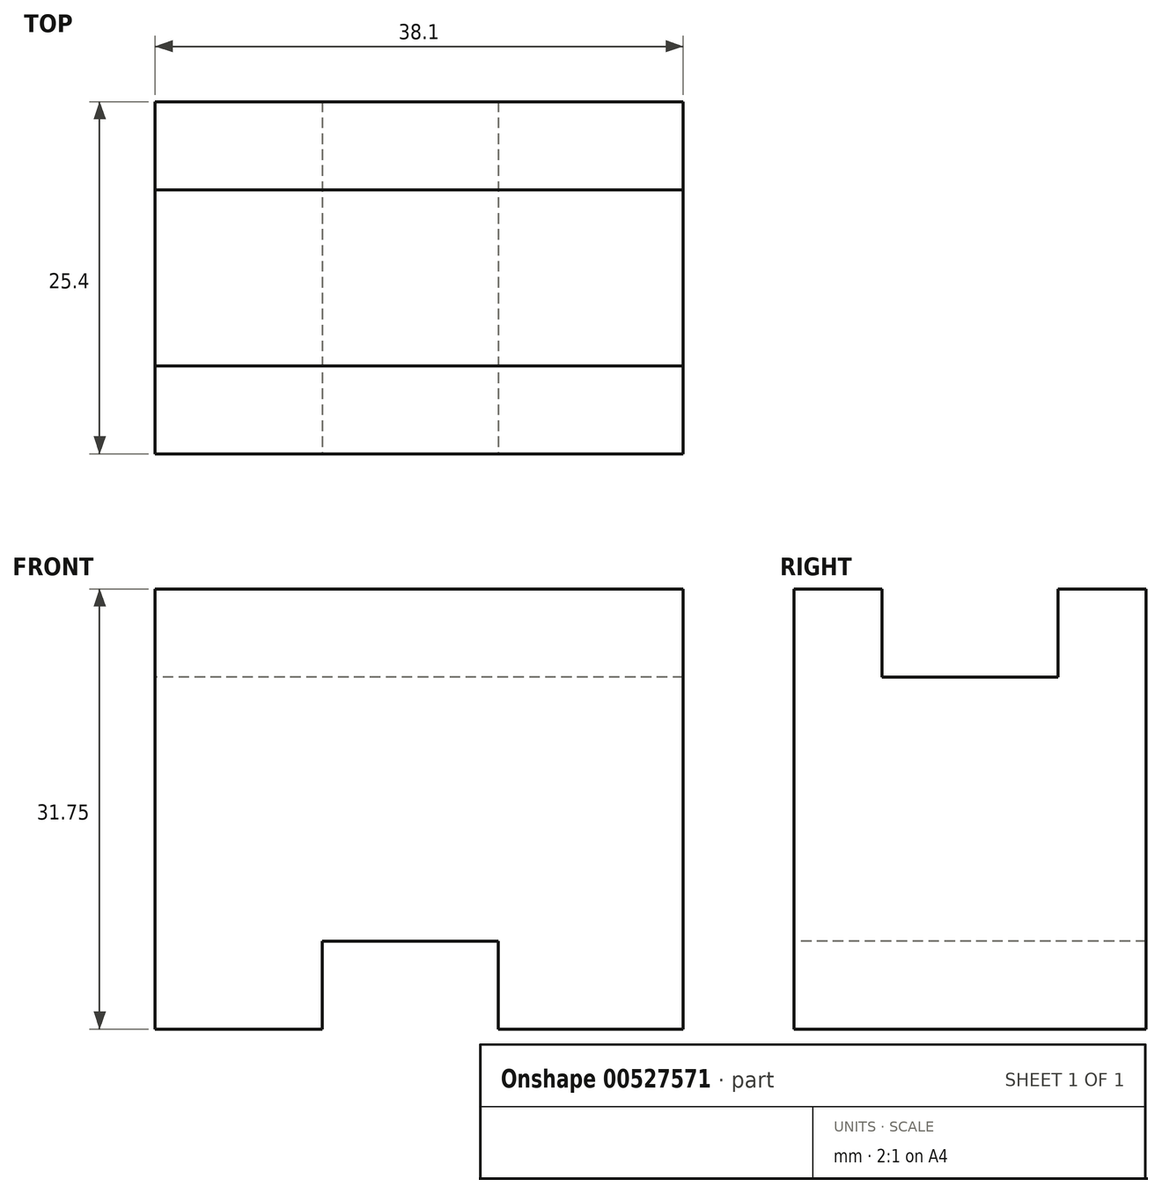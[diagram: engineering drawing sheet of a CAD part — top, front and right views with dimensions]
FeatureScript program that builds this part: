
annotation { "Feature Type Name" : "Feature", "Feature Type Description" : "" }
export const myFeature = defineFeature(function(context is Context, id is Id, definition is map)
    precondition{}
    {
        {
            var Q0;
            Q0=qCreatedBy(makeId("Right.planeOp"),FACE);
            var sketch = newSketch(context, id + "F0", { "sketchPlane" : qUnion([Q0])});
            skLineSegment(sketch, "E0", {"start": v(0, 0) * mm, "end": v(0, 31.75) * mm});
            skLineSegment(sketch, "E1", {"start": v(0, 31.75) * mm, "end": v(6.35, 31.75) * mm});
            skLineSegment(sketch, "E2", {"start": v(6.35, 31.75) * mm, "end": v(6.35, 25.4) * mm});
            skLineSegment(sketch, "E3", {"start": v(6.35, 25.4) * mm, "end": v(19.05, 25.4) * mm});
            skLineSegment(sketch, "E4", {"start": v(19.05, 25.4) * mm, "end": v(19.05, 31.75) * mm});
            skLineSegment(sketch, "E5", {"start": v(19.05, 31.75) * mm, "end": v(25.4, 31.75) * mm});
            skLineSegment(sketch, "E6", {"start": v(25.4, 31.75) * mm, "end": v(25.4, 0) * mm});
            skLineSegment(sketch, "E7", {"start": v(0, 0) * mm, "end": v(25.4, 0) * mm});
            skSolve(sketch);
        }
        {
            var Q0;
            Q0=makeQuery(id+"F0.imprint","IMPRINT",FACE,{"disambiguationData":[TD([[makeQuery(id+"F0.imprint","IMPRINT",EDGE,{"derivedFrom":sQuery(id+"F0.wireOp",EDGE,"E0")}),-1.0]])]});
            extrude(context, id + "F1", {"entities" : qUnion([Q0]), "depth" : 38.1 * mm, "offsetDistance" : 25.4 * mm});
        }
        {
            var Q0;
            Q0=makeQuery(id+"F1.opExtrude","SWEPT_FACE",FACE,{"disambiguationData":[OSD([sQuery(id+"F0.wireOp",EDGE,"E0")])]});
            var sketch = newSketch(context, id + "F2", { "sketchPlane" : qUnion([Q0])});
            skLineSegment(sketch, "E8", {"start": v(12.07, 0) * mm, "end": v(12.07, 6.35) * mm});
            skLineSegment(sketch, "E9", {"start": v(12.07, 6.35) * mm, "end": v(24.77, 6.35) * mm});
            skLineSegment(sketch, "E10", {"start": v(24.77, 6.35) * mm, "end": v(24.77, 0) * mm});
            skSolve(sketch);
        }
        {
            var Q0;
            {var subQ0=sQuery(id+"F2.wireOp",EDGE,"E8");Q0=makeQuery(id+"F2.imprint","IMPRINT",FACE,{"disambiguationData":[TD([[makeQuery(id+"F2.imprint","IMPRINT",EDGE,{"derivedFrom":subQ0}),-1.0]])]});}
            extrude(context, id + "F3", {"entities" : qUnion([Q0]), "operationType" : NewBodyOperationType.REMOVE, "oppositeDirection" : true, "depth" : 25.4 * mm, "offsetDistance" : 25.4 * mm});
        }
    });
